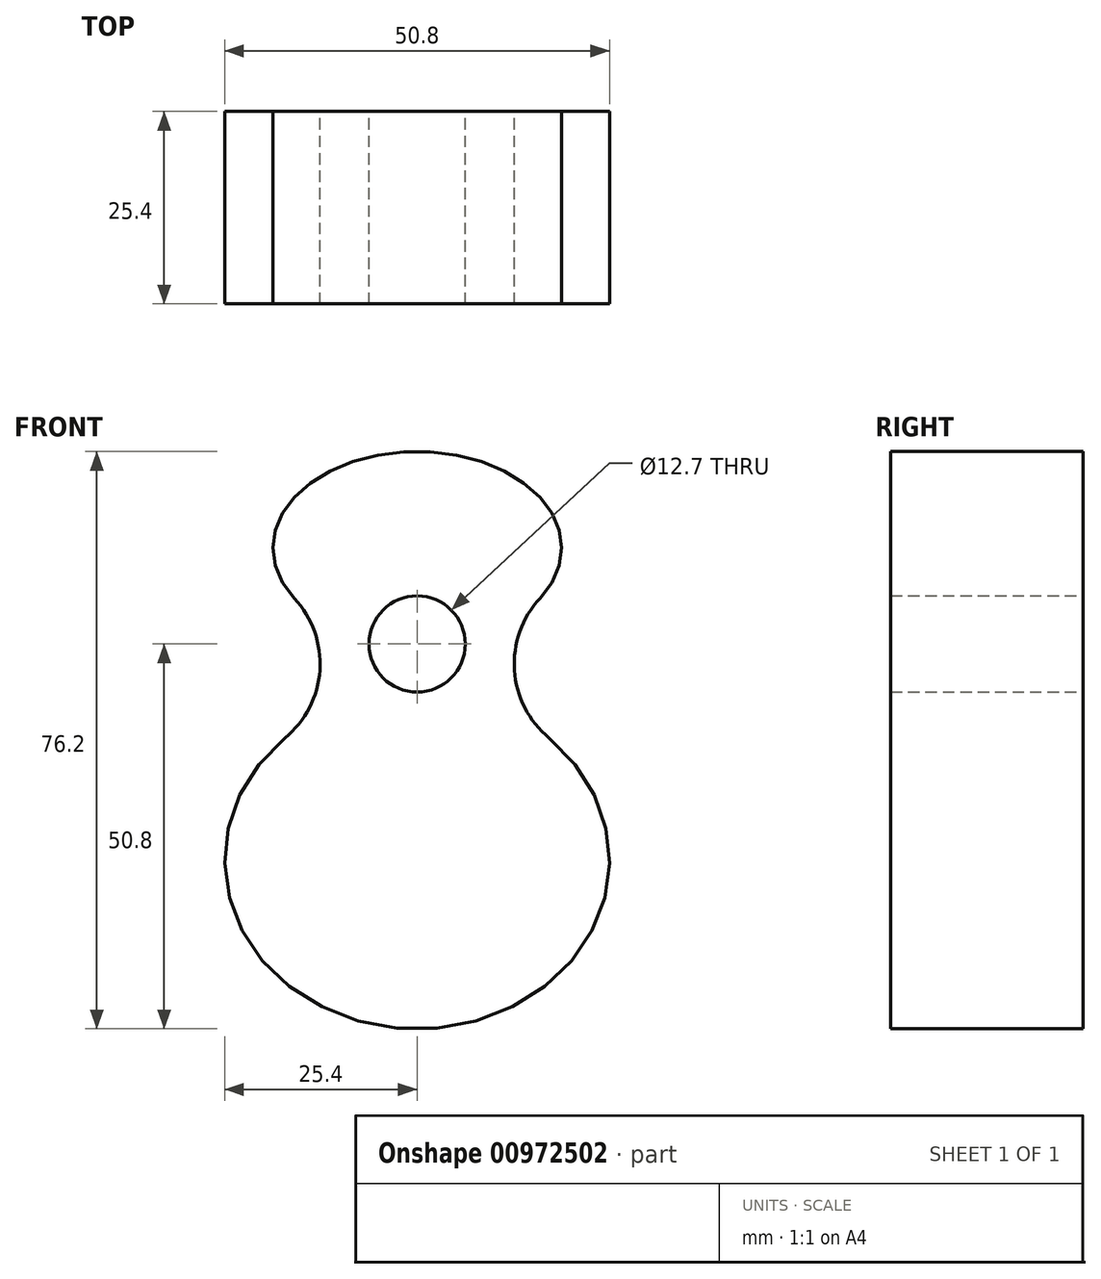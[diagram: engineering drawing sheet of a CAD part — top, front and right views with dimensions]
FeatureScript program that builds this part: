
annotation { "Feature Type Name" : "Feature", "Feature Type Description" : "" }
export const myFeature = defineFeature(function(context is Context, id is Id, definition is map)
    precondition{}
    {
        {
            var Q0;
            Q0=qCreatedBy(makeId("Front.planeOp"),FACE);
            var sketch = newSketch(context, id + "F0", { "sketchPlane" : qUnion([Q0])});
            skLineSegment(sketch, "E0", {"start": v(0, 0) * mm, "end": v(0, 50.8) * mm});
            skCircle(sketch, "E1", {"center": v(0, 50.8) * mm, "radius": 6.35 * mm});
            skLineSegment(sketch, "E2", {"start": v(0, 0) * mm, "end": v(22.03, 0) * mm});
            skLineSegment(sketch, "E3", {"start": v(0, 50.8) * mm, "end": v(12.7, 50.8) * mm});
            skLineSegment(sketch, "E4", {"start": v(0, 50.8) * mm, "end": v(0, 76.2) * mm});
            skLineSegment(sketch, "E5", {"start": v(0, 63.5) * mm, "end": v(19.05, 63.5) * mm});
            skLineSegment(sketch, "E6", {"start": v(0, 0) * mm, "end": v(0, 22.23) * mm});
            skLineSegment(sketch, "E7", {"start": v(0, 22.23) * mm, "end": v(25.4, 22.23) * mm});
            skEllipse(sketch, "E8", {"center": v(0, 63.5) * mm, "majorRadius": 19.05 * mm, "minorRadius": 12.7 * mm, "majorAxis": v(1, 0)});
            skEllipse(sketch, "E9", {"center": v(0, 22.23) * mm, "majorRadius": 22.23 * mm, "minorRadius": 25.4 * mm, "majorAxis": v(0, -1)});
            skCircle(sketch, "E10", {"center": v(25.51, 48.19) * mm, "radius": 12.7 * mm});
            skCircle(sketch, "E11.MirrorC", {"center": v(-25.51, 48.19) * mm, "radius": 12.7 * mm});
            skSolve(sketch);
        }
        {
            var Q0;
            {var subQ0=sQuery(id+"F0.wireOp",EDGE,"E0");var subQ1=makeQuery(id+"F0.imprint","INTERSECT",VERTEX,{"derivedFrom":[subQ0,sQuery(id+"F0.wireOp",EDGE,"E7")]});Q0=makeQuery(id+"F0.imprint","IMPRINT",FACE,{"disambiguationData":[TD([[makeQuery(id+"F0.imprint","IMPRINT",EDGE,{"disambiguationData":[TD([[subQ1,1.0]])],"derivedFrom":subQ0}),1.0]])]});}
            var Q1;
            {var subQ0=sQuery(id+"F0.wireOp",EDGE,"E7");Q1=makeQuery(id+"F0.imprint","IMPRINT",FACE,{"disambiguationData":[TD([[makeQuery(id+"F0.imprint","IMPRINT",EDGE,{"derivedFrom":subQ0}),-1.0]])]});}
            var Q2;
            {var subQ0=sQuery(id+"F0.wireOp",EDGE,"E7");Q2=makeQuery(id+"F0.imprint","IMPRINT",FACE,{"disambiguationData":[TD([[makeQuery(id+"F0.imprint","IMPRINT",EDGE,{"derivedFrom":subQ0}),1.0]])]});}
            var Q3;
            {var subQ3=sQuery(id+"F0.wireOp",EDGE,"E1");var subQ8=makeQuery(id+"F0.imprint","INTERSECT",VERTEX,{"derivedFrom":[subQ3,sQuery(id+"F0.wireOp",EDGE,"E3")]});Q3=makeQuery(id+"F0.imprint","IMPRINT",FACE,{"disambiguationData":[TD([[makeQuery(id+"F0.imprint","IMPRINT",EDGE,{"disambiguationData":[TD([[subQ8,-1.0]])],"derivedFrom":subQ3}),-1.0]])]});}
            var Q4;
            {var subQ0=sQuery(id+"F0.wireOp",EDGE,"E8");var subQ5=sQuery(id+"F0.wireOp",EDGE,"E11.MirrorC");var subQ6=makeQuery(id+"F0.imprint","INTERSECT",VERTEX,{"derivedFrom":[subQ0,subQ5]});Q4=makeQuery(id+"F0.imprint","IMPRINT",FACE,{"disambiguationData":[TD([[makeQuery(id+"F0.imprint","IMPRINT",EDGE,{"disambiguationData":[TD([[subQ6,-1.0]])],"derivedFrom":subQ0}),-1.0]])]});}
            var Q5;
            {var subQ4=sQuery(id+"F0.wireOp",EDGE,"E5");Q5=makeQuery(id+"F0.imprint","IMPRINT",FACE,{"disambiguationData":[TD([[makeQuery(id+"F0.imprint","IMPRINT",EDGE,{"derivedFrom":subQ4}),-1.0]])]});}
            var Q6;
            {var subQ0=sQuery(id+"F0.wireOp",EDGE,"E5");Q6=makeQuery(id+"F0.imprint","IMPRINT",FACE,{"disambiguationData":[TD([[makeQuery(id+"F0.imprint","IMPRINT",EDGE,{"derivedFrom":subQ0}),1.0]])]});}
            var Q7;
            {var subQ1=sQuery(id+"F0.wireOp",EDGE,"E4");var subQ5=sQuery(id+"F0.wireOp",EDGE,"E1");var subQ6=makeQuery(id+"F0.imprint","INTERSECT",VERTEX,{"derivedFrom":[subQ5,subQ1]});Q7=makeQuery(id+"F0.imprint","IMPRINT",FACE,{"disambiguationData":[TD([[makeQuery(id+"F0.imprint","IMPRINT",EDGE,{"disambiguationData":[TD([[subQ6,-1.0]])],"derivedFrom":subQ5}),-1.0]])]});}
            extrude(context, id + "F1", {"entities" : qUnion([Q0, Q1, Q2, Q3, Q4, Q5, Q6, Q7]), "depth" : 25.4 * mm, "offsetDistance" : 25.4 * mm});
        }
    });
